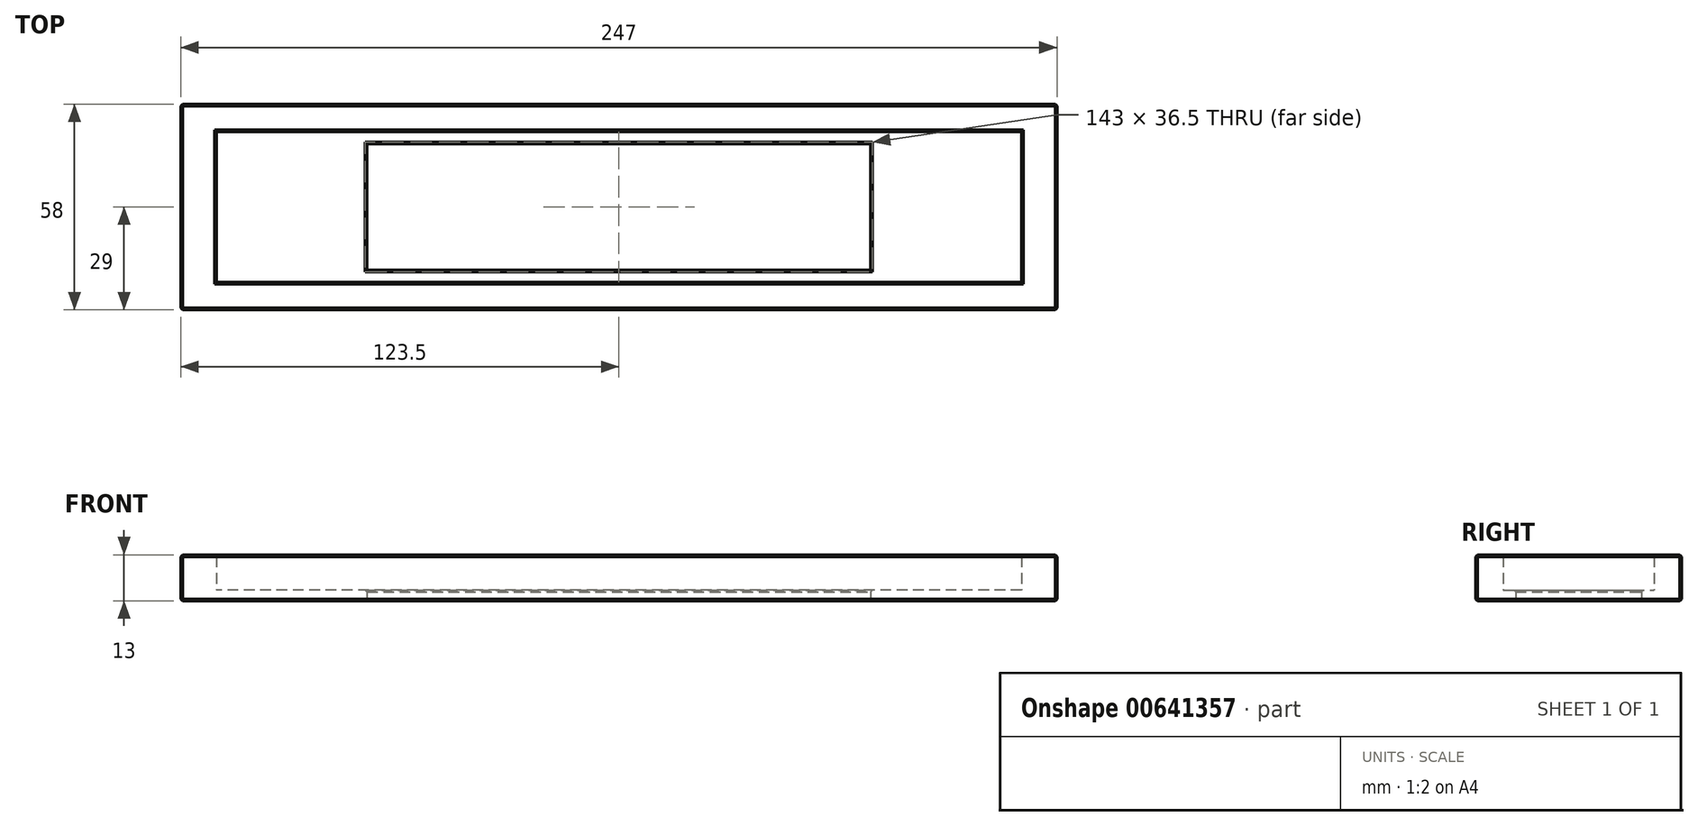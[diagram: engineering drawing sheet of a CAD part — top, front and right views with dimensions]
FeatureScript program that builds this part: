
annotation { "Feature Type Name" : "Feature", "Feature Type Description" : "" }
export const myFeature = defineFeature(function(context is Context, id is Id, definition is map)
    precondition{}
    {
        {
            var Q0;
            Q0=qCreatedBy(makeId("Top.planeOp"),FACE);
            var sketch = newSketch(context, id + "F0", { "sketchPlane" : qUnion([Q0])});
            skLineSegment(sketch, "E0.bottom", {"start": v(71, -17.75) * mm, "end": v(-71, -17.75) * mm});
            skLineSegment(sketch, "E0.top", {"start": v(71, 17.75) * mm, "end": v(-71, 17.75) * mm});
            skLineSegment(sketch, "E0.left", {"start": v(71, -17.75) * mm, "end": v(71, 17.75) * mm});
            skLineSegment(sketch, "E0.right", {"start": v(-71, -17.75) * mm, "end": v(-71, 17.75) * mm});
            skPoint(sketch, "E0.middle", {"position": v(0, 0) * mm});
            skLineSegment(sketch, "E1.bottom", {"start": v(113.5, -21.25) * mm, "end": v(-113.5, -21.25) * mm});
            skLineSegment(sketch, "E1.top", {"start": v(113.5, 21.25) * mm, "end": v(-113.5, 21.25) * mm});
            skLineSegment(sketch, "E1.left", {"start": v(113.5, -21.25) * mm, "end": v(113.5, 21.25) * mm});
            skLineSegment(sketch, "E1.right", {"start": v(-113.5, -21.25) * mm, "end": v(-113.5, 21.25) * mm});
            skLineSegment(sketch, "E2.bottom", {"start": v(123.5, -29) * mm, "end": v(-123.5, -29) * mm});
            skLineSegment(sketch, "E2.top", {"start": v(123.5, 29) * mm, "end": v(-123.5, 29) * mm});
            skLineSegment(sketch, "E2.left", {"start": v(123.5, -29) * mm, "end": v(123.5, 29) * mm});
            skLineSegment(sketch, "E2.right", {"start": v(-123.5, -29) * mm, "end": v(-123.5, 29) * mm});
            skSolve(sketch);
        }
        {
            var Q0;
            Q0=makeQuery(id+"F0.imprint","IMPRINT",FACE,{"disambiguationData":[TD([[makeQuery(id+"F0.imprint","IMPRINT",EDGE,{"derivedFrom":sQuery(id+"F0.wireOp",EDGE,"E0.bottom")}),1.0]])]});
            extrude(context, id + "F1", {"entities" : qUnion([Q0]), "depth" : 3 * mm, "offsetDistance" : 25 * mm});
        }
        {
            var Q0;
            Q0=makeQuery(id+"F0.imprint","IMPRINT",FACE,{"disambiguationData":[TD([[makeQuery(id+"F0.imprint","IMPRINT",EDGE,{"derivedFrom":sQuery(id+"F0.wireOp",EDGE,"E1.bottom")}),1.0]])]});
            extrude(context, id + "F2", {"entities" : qUnion([Q0]), "operationType" : NewBodyOperationType.ADD, "depth" : 13 * mm, "offsetDistance" : 25 * mm});
        }
        {
            var Q0;
            Q0=makeQuery(id+"F2.opExtrude","SWEPT_EDGE",EDGE,{"disambiguationData":[OSD([sQuery(id+"F0.wireOp",EDGE,"E2.bottom"),sQuery(id+"F0.wireOp",EDGE,"E2.right")])]});
            var Q1;
            Q1=makeQuery(id+"F2.opExtrude","CAP_FACE",FACE,{"disambiguationData":[OSD([sQuery(id+"F0.wireOp",EDGE,"E1.bottom"),sQuery(id+"F0.wireOp",EDGE,"E1.top"),sQuery(id+"F0.wireOp",EDGE,"E1.left"),sQuery(id+"F0.wireOp",EDGE,"E1.right"),sQuery(id+"F0.wireOp",EDGE,"E2.bottom"),sQuery(id+"F0.wireOp",EDGE,"E2.top"),sQuery(id+"F0.wireOp",EDGE,"E2.left"),sQuery(id+"F0.wireOp",EDGE,"E2.right")])],"isStart":false});
            var Q2;
            Q2=makeQuery(id+"F2.opExtrude","SWEPT_EDGE",EDGE,{"disambiguationData":[OSD([sQuery(id+"F0.wireOp",EDGE,"E2.bottom"),sQuery(id+"F0.wireOp",EDGE,"E2.left")])]});
            var Q3;
            Q3=makeQuery(id+"F2.opExtrude","SWEPT_EDGE",EDGE,{"disambiguationData":[OSD([sQuery(id+"F0.wireOp",EDGE,"E2.top"),sQuery(id+"F0.wireOp",EDGE,"E2.left")])]});
            var Q4;
            Q4=makeQuery(id+"F2.opExtrude","SWEPT_EDGE",EDGE,{"disambiguationData":[OSD([sQuery(id+"F0.wireOp",EDGE,"E2.top"),sQuery(id+"F0.wireOp",EDGE,"E2.right")])]});
            var Q5;
            Q5=makeQuery(id+"F2.opExtrude","CAP_EDGE",EDGE,{"disambiguationData":[OSD([sQuery(id+"F0.wireOp",EDGE,"E2.right")])],"isStart":true});
            var Q6;
            Q6=makeQuery(id+"F2.opExtrude","CAP_EDGE",EDGE,{"disambiguationData":[OSD([sQuery(id+"F0.wireOp",EDGE,"E2.bottom")])],"isStart":true});
            var Q7;
            Q7=makeQuery(id+"F2.opExtrude","CAP_EDGE",EDGE,{"disambiguationData":[OSD([sQuery(id+"F0.wireOp",EDGE,"E2.top")])],"isStart":true});
            var Q8;
            Q8=makeQuery(id+"F2.opExtrude","CAP_EDGE",EDGE,{"disambiguationData":[OSD([sQuery(id+"F0.wireOp",EDGE,"E2.left")])],"isStart":true});
            chamfer(context, id + "F3", {"entities" : qUnion([Q0, Q1, Q2, Q3, Q4, Q5, Q6, Q7, Q8]), "width" : .5 * mm, "tangentPropagation" : true});
        }
        {
            var Q0;
            Q0=makeQuery(id+"F1.opExtrude","CAP_EDGE",EDGE,{"disambiguationData":[OSD([sQuery(id+"F0.wireOp",EDGE,"E0.bottom")])],"isStart":false});
            var Q1;
            Q1=makeQuery(id+"F1.opExtrude","CAP_EDGE",EDGE,{"disambiguationData":[OSD([sQuery(id+"F0.wireOp",EDGE,"E0.right")])],"isStart":false});
            var Q2;
            Q2=makeQuery(id+"F1.opExtrude","CAP_EDGE",EDGE,{"disambiguationData":[OSD([sQuery(id+"F0.wireOp",EDGE,"E0.top")])],"isStart":false});
            var Q3;
            Q3=makeQuery(id+"F1.opExtrude","CAP_EDGE",EDGE,{"disambiguationData":[OSD([sQuery(id+"F0.wireOp",EDGE,"E0.left")])],"isStart":false});
            var Q4;
            Q4=makeQuery(id+"F1.opExtrude","CAP_EDGE",EDGE,{"disambiguationData":[OSD([sQuery(id+"F0.wireOp",EDGE,"E0.bottom")])],"isStart":true});
            var Q5;
            Q5=makeQuery(id+"F1.opExtrude","CAP_EDGE",EDGE,{"disambiguationData":[OSD([sQuery(id+"F0.wireOp",EDGE,"E0.right")])],"isStart":true});
            var Q6;
            Q6=makeQuery(id+"F1.opExtrude","CAP_EDGE",EDGE,{"disambiguationData":[OSD([sQuery(id+"F0.wireOp",EDGE,"E0.top")])],"isStart":true});
            var Q7;
            Q7=makeQuery(id+"F1.opExtrude","CAP_EDGE",EDGE,{"disambiguationData":[OSD([sQuery(id+"F0.wireOp",EDGE,"E0.left")])],"isStart":true});
            chamfer(context, id + "F4", {"entities" : qUnion([Q0, Q1, Q2, Q3, Q4, Q5, Q6, Q7]), "width" : .5 * mm, "tangentPropagation" : true});
        }
    });
